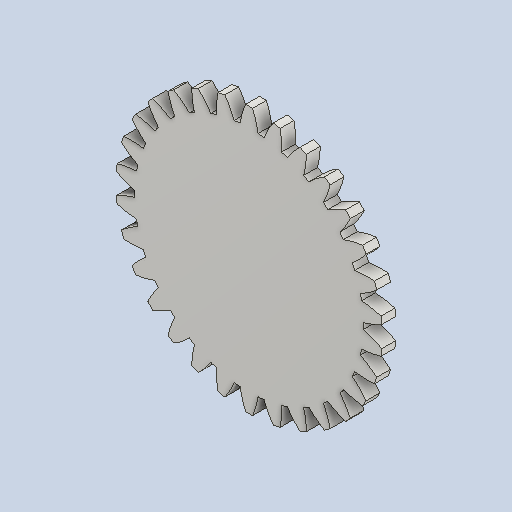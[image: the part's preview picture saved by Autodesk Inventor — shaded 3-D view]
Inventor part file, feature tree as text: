
AUTODESK INVENTOR PART (.ipt)
format: ipt  version: 2022 (Build 260153000, 153)  size: 267,776 bytes
history: native  units: mm (DEFAULTED — no unit token found)
features: plane x3, other x3, sketch x2, extrude x1
ambient origin geometry x8: Origin, YZ Plane, XZ Plane, XY Plane, X Axis, Y Axis, Z Axis, Center Point
bodies: Solid1 (feature_tree)
feature tree (9):
  extrude  "Extrusion1"  Depth=5.0mm TaperAngle=0.0deg
  plane  "Work Plane2"
  plane  "Work Plane8"
  plane  "Work Plane9"
  other  "Spur Gear"
  sketch  "Sketch1"  dims[d0=96.0mm d1=5.0mm d2=0.0mm]
  sketch  "Sketch2"  dims[d3=90.0mm d4=10.0mm d5=0.0mm d16=90.0mm d17=0.0mm d34=1.047198mm d39=0.0mm d41=0.0mm d43=90.0mm d46=90.0mm d47=0.0mm d48=0.0mm]
  other  "Srf1"
  other  "Pitch Diameter"
